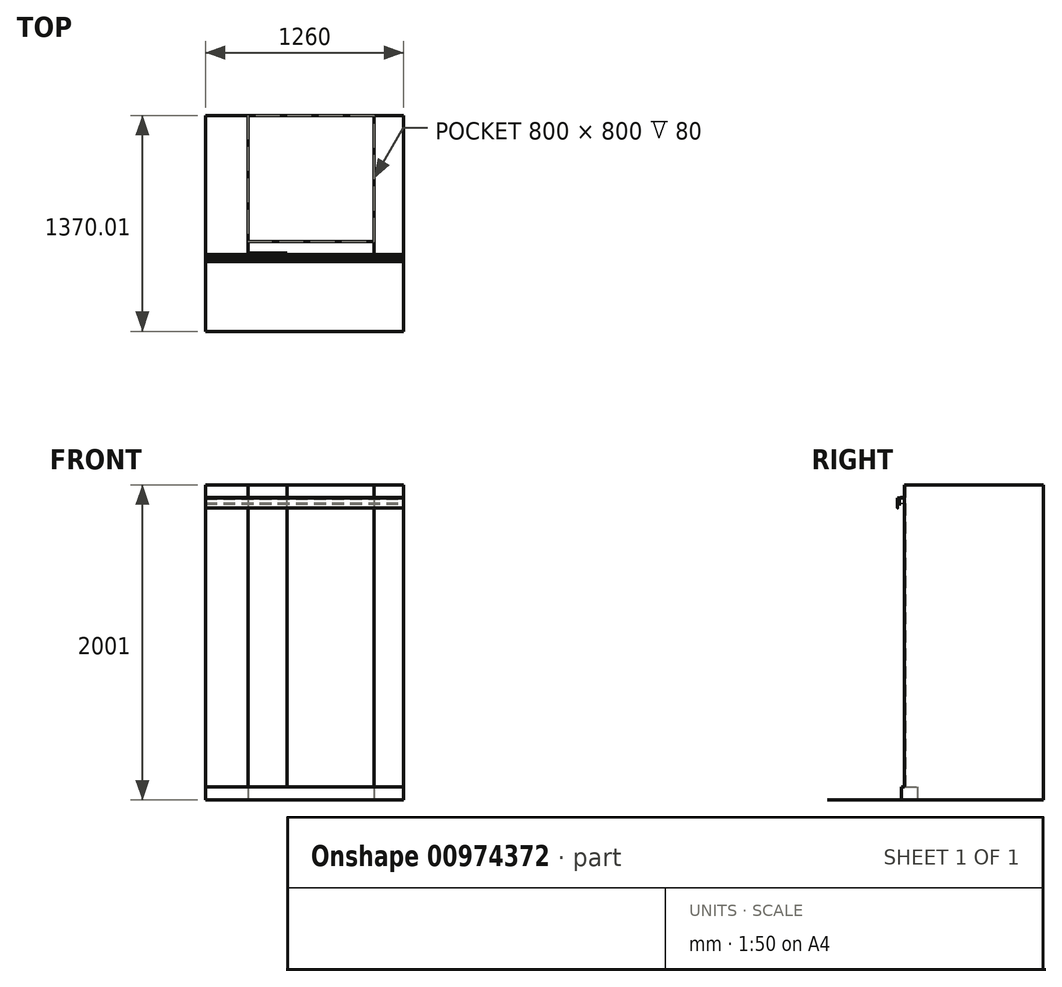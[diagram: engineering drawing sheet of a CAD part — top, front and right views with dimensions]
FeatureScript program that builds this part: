
annotation { "Feature Type Name" : "Feature", "Feature Type Description" : "" }
export const myFeature = defineFeature(function(context is Context, id is Id, definition is map)
    precondition{}
    {
        {
            var Q0;
            Q0=qCreatedBy(makeId("Top.planeOp"),FACE);
            var sketch = newSketch(context, id + "F0", { "sketchPlane" : qUnion([Q0])});
            skLineSegment(sketch, "E0", {"start": v(-511.66, 0) * mm, "end": v(748.34, 0) * mm});
            skLineSegment(sketch, "E1", {"start": v(748.34, 0) * mm, "end": v(748.34, 20) * mm});
            skLineSegment(sketch, "E2", {"start": v(748.34, 20) * mm, "end": v(558.34, 20) * mm});
            skLineSegment(sketch, "E3", {"start": v(558.34, 20) * mm, "end": v(558.34, 100) * mm});
            skLineSegment(sketch, "E4", {"start": v(558.34, 100) * mm, "end": v(-241.66, 100) * mm});
            skLineSegment(sketch, "E5", {"start": v(-241.66, 100) * mm, "end": v(-241.66, 20) * mm});
            skLineSegment(sketch, "E6", {"start": v(-241.66, 20) * mm, "end": v(-511.66, 20) * mm});
            skLineSegment(sketch, "E7", {"start": v(-511.66, 20) * mm, "end": v(-511.66, 0) * mm});
            skSolve(sketch);
        }
        {
            var Q0;
            Q0=makeQuery(id+"F0.imprint","IMPRINT",FACE,{"disambiguationData":[TD([[makeQuery(id+"F0.imprint","IMPRINT",EDGE,{"derivedFrom":sQuery(id+"F0.wireOp",EDGE,"E0")}),1.0]])]});
            extrude(context, id + "F1", {"entities" : qUnion([Q0]), "depth" : 80 * mm, "offsetDistance" : 25 * mm});
        }
        {
            var Q0;
            Q0=makeQuery(id+"F1.opExtrude","CAP_FACE",FACE,{"disambiguationData":[OSD([sQuery(id+"F0.wireOp",EDGE,"E0"),sQuery(id+"F0.wireOp",EDGE,"E1"),sQuery(id+"F0.wireOp",EDGE,"E2"),sQuery(id+"F0.wireOp",EDGE,"E3"),sQuery(id+"F0.wireOp",EDGE,"E4"),sQuery(id+"F0.wireOp",EDGE,"E5"),sQuery(id+"F0.wireOp",EDGE,"E6"),sQuery(id+"F0.wireOp",EDGE,"E7")])],"isStart":true});
            var sketch = newSketch(context, id + "F2", { "sketchPlane" : qUnion([Q0])});
            skLineSegment(sketch, "E8.bottom", {"start": v(-511.66, -900) * mm, "end": v(748.34, -900) * mm});
            skLineSegment(sketch, "E8.top", {"start": v(-511.66, 469.01) * mm, "end": v(748.34, 469.01) * mm});
            skLineSegment(sketch, "E8.left", {"start": v(-511.66, -900) * mm, "end": v(-511.66, 469.01) * mm});
            skLineSegment(sketch, "E8.right", {"start": v(748.34, -900) * mm, "end": v(748.34, 469.01) * mm});
            skSolve(sketch);
        }
        {
            var Q0;
            Q0 = qSketchRegion(id + "F2", true);
            extrude(context, id + "F3", {"entities" : qUnion([Q0]), "operationType" : NewBodyOperationType.ADD, "depth" : 1 * mm, "offsetDistance" : 25 * mm});
        }
        {
            var Q0;
            {var subQ0=sQuery(id+"F2.wireOp",EDGE,"E8.right");var subQ1=sQuery(id+"F2.wireOp",EDGE,"E8.left");var subQ2=sQuery(id+"F2.wireOp",EDGE,"E8.bottom");Q0=makeQuery(id+"F3.boolean.opBoolean","SPLIT",FACE,{"disambiguationData":[TD([makeQuery(id+"F1.opExtrude","SWEPT_FACE",FACE,{"disambiguationData":[OSD([sQuery(id+"F0.wireOp",EDGE,"E2")])]})])],"derivedFrom":makeQuery(id+"F3.opExtrude","CAP_FACE",FACE,{"disambiguationData":[OSD([subQ2,sQuery(id+"F2.wireOp",EDGE,"E8.top"),subQ1,subQ0])],"isStart":true})});}
            var sketch = newSketch(context, id + "F4", { "sketchPlane" : qUnion([Q0])});
            skLineSegment(sketch, "E9.bottom", {"start": v(-511.66, 20) * mm, "end": v(-241.66, 20) * mm});
            skLineSegment(sketch, "E9.top", {"start": v(-511.66, 900) * mm, "end": v(-241.66, 900) * mm});
            skLineSegment(sketch, "E9.left", {"start": v(-511.66, 20) * mm, "end": v(-511.66, 900) * mm});
            skLineSegment(sketch, "E9.right", {"start": v(-241.66, 20) * mm, "end": v(-241.66, 900) * mm});
            skLineSegment(sketch, "E10.bottom", {"start": v(748.34, 20) * mm, "end": v(558.34, 20) * mm});
            skLineSegment(sketch, "E10.top", {"start": v(748.34, 900) * mm, "end": v(558.34, 900) * mm});
            skLineSegment(sketch, "E10.left", {"start": v(748.34, 20) * mm, "end": v(748.34, 900) * mm});
            skLineSegment(sketch, "E10.right", {"start": v(558.34, 20) * mm, "end": v(558.34, 900) * mm});
            skSolve(sketch);
        }
        {
            var Q0;
            Q0 = qSketchRegion(id + "F4", true);
            extrude(context, id + "F5", {"entities" : qUnion([Q0]), "operationType" : NewBodyOperationType.ADD, "depth" : 2000 * mm, "offsetDistance" : 25 * mm});
        }
        {
            var Q0;
            Q0=makeQuery(id+"F5.boolean.opBoolean","MERGE",FACE,{"derivedFrom":[makeQuery(id+"F3.opExtrude","SWEPT_FACE",FACE,{"disambiguationData":[OSD([sQuery(id+"F2.wireOp",EDGE,"E8.bottom")])]}),makeQuery(id+"F5.opExtrude","SWEPT_FACE",FACE,{"disambiguationData":[OSD([sQuery(id+"F4.wireOp",EDGE,"E9.top")])]}),makeQuery(id+"F5.opExtrude","SWEPT_FACE",FACE,{"disambiguationData":[OSD([sQuery(id+"F4.wireOp",EDGE,"E10.top")])]})]});
            var sketch = newSketch(context, id + "F6", { "sketchPlane" : qUnion([Q0])});
            skLineSegment(sketch, "E11.bottom", {"start": v(-748.34, -1) * mm, "end": v(511.66, -1) * mm});
            skLineSegment(sketch, "E11.top", {"start": v(-748.34, 2000) * mm, "end": v(511.66, 2000) * mm});
            skLineSegment(sketch, "E11.left", {"start": v(-748.34, -1) * mm, "end": v(-748.34, 2000) * mm});
            skLineSegment(sketch, "E11.right", {"start": v(511.66, -1) * mm, "end": v(511.66, 2000) * mm});
            skSolve(sketch);
        }
        {
            var Q0;
            Q0 = qSketchRegion(id + "F6", true);
            extrude(context, id + "F7", {"entities" : qUnion([Q0]), "operationType" : NewBodyOperationType.ADD, "depth" : 1 * mm, "offsetDistance" : 25 * mm});
        }
        {
            var Q0;
            Q0=makeQuery(id+"F7.boolean.opBoolean","MERGE",FACE,{"derivedFrom":[makeQuery(id+"F5.opExtrude","CAP_FACE",FACE,{"disambiguationData":[OSD([sQuery(id+"F4.wireOp",EDGE,"E9.bottom"),sQuery(id+"F4.wireOp",EDGE,"E9.top"),sQuery(id+"F4.wireOp",EDGE,"E9.left"),sQuery(id+"F4.wireOp",EDGE,"E9.right")])],"isStart":false}),makeQuery(id+"F5.opExtrude","CAP_FACE",FACE,{"disambiguationData":[OSD([sQuery(id+"F4.wireOp",EDGE,"E10.bottom"),sQuery(id+"F4.wireOp",EDGE,"E10.top"),sQuery(id+"F4.wireOp",EDGE,"E10.left"),sQuery(id+"F4.wireOp",EDGE,"E10.right")])],"isStart":false}),makeQuery(id+"F7.opExtrude","SWEPT_FACE",FACE,{"disambiguationData":[OSD([sQuery(id+"F6.wireOp",EDGE,"E11.top")])]})]});
            var sketch = newSketch(context, id + "F8", { "sketchPlane" : qUnion([Q0])});
            skLineSegment(sketch, "E12.bottom", {"start": v(748.34, 901) * mm, "end": v(-511.66, 901) * mm});
            skLineSegment(sketch, "E12.top", {"start": v(748.34, -467.34) * mm, "end": v(-511.66, -467.34) * mm});
            skLineSegment(sketch, "E12.left", {"start": v(748.34, 901) * mm, "end": v(748.34, -467.34) * mm});
            skLineSegment(sketch, "E12.right", {"start": v(-511.66, 901) * mm, "end": v(-511.66, -467.34) * mm});
            skSolve(sketch);
        }
        {
            var Q0;
            Q0=makeQuery(id+"FwCDVaagBMNMzfp_1.boolean.opBoolean","MERGE",FACE,{"derivedFrom":[makeQuery(id+"F7.boolean.opBoolean","MERGE",FACE,{"derivedFrom":[makeQuery(id+"F5.boolean.opBoolean","MERGE",FACE,{"derivedFrom":[makeQuery(id+"F3.boolean.opBoolean","MERGE",FACE,{"derivedFrom":[makeQuery(id+"F1.opExtrude","SWEPT_FACE",FACE,{"disambiguationData":[OSD([sQuery(id+"F0.wireOp",EDGE,"E1")])]}),makeQuery(id+"F3.opExtrude","SWEPT_FACE",FACE,{"disambiguationData":[OSD([sQuery(id+"F2.wireOp",EDGE,"E8.right")])]})]}),makeQuery(id+"F5.opExtrude","SWEPT_FACE",FACE,{"disambiguationData":[OSD([sQuery(id+"F4.wireOp",EDGE,"E10.left")])]})]}),makeQuery(id+"F7.opExtrude","SWEPT_FACE",FACE,{"disambiguationData":[OSD([sQuery(id+"F6.wireOp",EDGE,"E11.left")])]})]}),makeQuery(id+"FwCDVaagBMNMzfp_1.opExtrude","SWEPT_FACE",FACE,{"disambiguationData":[OSD([sQuery(id+"F8.wireOp",EDGE,"E12.left")])]})]});
            var sketch = newSketch(context, id + "F9", { "sketchPlane" : qUnion([Q0])});
            skLineSegment(sketch, "E13", {"start": v(3, 1919) * mm, "end": v(3, 1916) * mm, "construction": true});
            skLineSegment(sketch, "E14", {"start": v(-4, 1916) * mm, "end": v(-4, 1914) * mm});
            skLineSegment(sketch, "E15", {"start": v(-4, 1914) * mm, "end": v(-14, 1914) * mm});
            skLineSegment(sketch, "E16", {"start": v(-14, 1914) * mm, "end": v(-14, 1880) * mm});
            skLineSegment(sketch, "E17", {"start": v(-2, 1880) * mm, "end": v(-2, 1886.01) * mm});
            skLineSegment(sketch, "E18", {"start": v(-7, 1919) * mm, "end": v(-7, 1916) * mm});
            skLineSegment(sketch, "E19", {"start": v(-7, 1916) * mm, "end": v(-4, 1916) * mm});
            skLineSegment(sketch, "E20", {"start": v(-7, 1919) * mm, "end": v(3, 1919) * mm});
            skLineSegment(sketch, "E21", {"start": v(3, 1916) * mm, "end": v(-2, 1916) * mm});
            skLineSegment(sketch, "E22", {"start": v(-2, 1916) * mm, "end": v(-2, 1912) * mm});
            skLineSegment(sketch, "E23", {"start": v(-2, 1912) * mm, "end": v(-12, 1912) * mm});
            skLineSegment(sketch, "E24", {"start": v(-12, 1912) * mm, "end": v(-12, 1882) * mm});
            skLineSegment(sketch, "E25", {"start": v(-12, 1882) * mm, "end": v(-4, 1882) * mm});
            skLineSegment(sketch, "E26", {"start": v(-4, 1882) * mm, "end": v(-4, 1886.01) * mm});
            skLineSegment(sketch, "E27", {"start": v(-2, 1886.01) * mm, "end": v(-4, 1886.01) * mm});
            skLineSegment(sketch, "E28", {"start": v(-14, 1880) * mm, "end": v(-2, 1880) * mm});
            skLineSegment(sketch, "E29.MirrorCS", {"start": v(8, 1886.01) * mm, "end": v(10, 1886.01) * mm});
            skLineSegment(sketch, "E30.MirrorCS", {"start": v(13, 1919) * mm, "end": v(13, 1916) * mm});
            skLineSegment(sketch, "E31.MirrorCS", {"start": v(13, 1916) * mm, "end": v(10, 1916) * mm});
            skLineSegment(sketch, "E32.MirrorCS", {"start": v(10, 1916) * mm, "end": v(10, 1914) * mm});
            skLineSegment(sketch, "E33.MirrorCS", {"start": v(8, 1880) * mm, "end": v(8, 1886.01) * mm});
            skLineSegment(sketch, "E34.MirrorCS", {"start": v(10, 1882) * mm, "end": v(10, 1886.01) * mm});
            skLineSegment(sketch, "E35.MirrorCS", {"start": v(8, 1916) * mm, "end": v(8, 1912) * mm});
            skLineSegment(sketch, "E36.MirrorCS", {"start": v(18, 1912) * mm, "end": v(18, 1882) * mm});
            skLineSegment(sketch, "E37.MirrorCS", {"start": v(13, 1919) * mm, "end": v(3, 1919) * mm});
            skLineSegment(sketch, "E38.MirrorCS", {"start": v(20, 1880) * mm, "end": v(8, 1880) * mm});
            skLineSegment(sketch, "E39.MirrorCS", {"start": v(20, 1914) * mm, "end": v(20, 1880) * mm});
            skLineSegment(sketch, "E40.MirrorCS", {"start": v(18, 1882) * mm, "end": v(10, 1882) * mm});
            skLineSegment(sketch, "E41.MirrorCS", {"start": v(3, 1916) * mm, "end": v(8, 1916) * mm});
            skLineSegment(sketch, "E42.MirrorCS", {"start": v(8, 1912) * mm, "end": v(18, 1912) * mm});
            skLineSegment(sketch, "E43.MirrorCS", {"start": v(10, 1914) * mm, "end": v(20, 1914) * mm});
            skSolve(sketch);
        }
        {
            var Q0;
            Q0 = qSketchRegion(id + "F9", true);
            var Q1;
            Q1=makeQuery(id+"FwCDVaagBMNMzfp_1.boolean.opBoolean","MERGE",FACE,{"derivedFrom":[makeQuery(id+"F7.boolean.opBoolean","MERGE",FACE,{"derivedFrom":[makeQuery(id+"F5.boolean.opBoolean","MERGE",FACE,{"derivedFrom":[makeQuery(id+"F3.boolean.opBoolean","MERGE",FACE,{"derivedFrom":[makeQuery(id+"F1.opExtrude","SWEPT_FACE",FACE,{"disambiguationData":[OSD([sQuery(id+"F0.wireOp",EDGE,"E7")])]}),makeQuery(id+"F3.opExtrude","SWEPT_FACE",FACE,{"disambiguationData":[OSD([sQuery(id+"F2.wireOp",EDGE,"E8.left")])]})]}),makeQuery(id+"F5.opExtrude","SWEPT_FACE",FACE,{"disambiguationData":[OSD([sQuery(id+"F4.wireOp",EDGE,"E9.left")])]})]}),makeQuery(id+"F7.opExtrude","SWEPT_FACE",FACE,{"disambiguationData":[OSD([sQuery(id+"F6.wireOp",EDGE,"E11.right")])]})]}),makeQuery(id+"FwCDVaagBMNMzfp_1.opExtrude","SWEPT_FACE",FACE,{"disambiguationData":[OSD([sQuery(id+"F8.wireOp",EDGE,"E12.right")])]})]});
            extrude(context, id + "F10", {"entities" : qUnion([Q0]), "endBound" : BoundingType.UP_TO_SURFACE, "oppositeDirection" : true, "depth" : 25 * mm, "endBoundEntityFace" : qUnion([Q1]), "offsetDistance" : 25 * mm});
        }
        {
            var Q0;
            Q0=makeQuery(id+"F7.boolean.opBoolean","MERGE",FACE,{"derivedFrom":[makeQuery(id+"F5.boolean.opBoolean","MERGE",FACE,{"derivedFrom":[makeQuery(id+"F3.boolean.opBoolean","MERGE",FACE,{"derivedFrom":[makeQuery(id+"F1.opExtrude","SWEPT_FACE",FACE,{"disambiguationData":[OSD([sQuery(id+"F0.wireOp",EDGE,"E1")])]}),makeQuery(id+"F3.opExtrude","SWEPT_FACE",FACE,{"disambiguationData":[OSD([sQuery(id+"F2.wireOp",EDGE,"E8.right")])]})]}),makeQuery(id+"F5.opExtrude","SWEPT_FACE",FACE,{"disambiguationData":[OSD([sQuery(id+"F4.wireOp",EDGE,"E10.left")])]})]}),makeQuery(id+"F7.opExtrude","SWEPT_FACE",FACE,{"disambiguationData":[OSD([sQuery(id+"F6.wireOp",EDGE,"E11.left")])]})]});
            var sketch = newSketch(context, id + "F11", { "sketchPlane" : qUnion([Q0])});
            skLineSegment(sketch, "E44", {"start": v(-26.6, 1862.69) * mm, "end": v(-28.1, 1862.69) * mm, "construction": true});
            skArc(sketch, "E45.MirrorCS", {"start": v(-23.35, 1852.76) * mm, "mid": v(-23.34, 1852.6) * mm, "end": v(-23.42, 1852.45) * mm});
            skArc(sketch, "E46.MirrorCS", {"start": v(-24.12, 1851.75) * mm, "mid": v(-24.4, 1851.67) * mm, "end": v(-24.61, 1851.85) * mm});
            skLineSegment(sketch, "E47.MirrorCS", {"start": v(-24.12, 1851.75) * mm, "end": v(-23.42, 1852.45) * mm});
            skLineSegment(sketch, "E48.MirrorCS", {"start": v(-25.1, 1915.92) * mm, "end": v(-25.1, 1917.42) * mm});
            skLineSegment(sketch, "E49.MirrorCS", {"start": v(-17.1, 1883.42) * mm, "end": v(-15.6, 1883.42) * mm});
            skLineSegment(sketch, "E50.MirrorCS", {"start": v(-25.1, 1917.42) * mm, "end": v(-26.6, 1917.42) * mm});
            skLineSegment(sketch, "E51.MirrorCS", {"start": v(-26.6, 1862.69) * mm, "end": v(-25.1, 1862.69) * mm, "construction": true});
            skLineSegment(sketch, "E52.MirrorCS", {"start": v(-10.6, 1880.42) * mm, "end": v(-10.6, 1878.92) * mm});
            skLineSegment(sketch, "E53.MirrorCS", {"start": v(-15.6, 1914.42) * mm, "end": v(-15.6, 1911.42) * mm});
            skLineSegment(sketch, "E54.MirrorCS", {"start": v(-15.6, 1911.42) * mm, "end": v(-17.1, 1911.42) * mm});
            skLineSegment(sketch, "E55.MirrorCS", {"start": v(-10.6, 1914.42) * mm, "end": v(-10.6, 1915.92) * mm});
            skLineSegment(sketch, "E56.MirrorCS", {"start": v(-17.1, 1880.42) * mm, "end": v(-17.1, 1883.42) * mm});
            skLineSegment(sketch, "E57.MirrorCS", {"start": v(-15.6, 1883.42) * mm, "end": v(-15.6, 1880.42) * mm});
            skLineSegment(sketch, "E58.MirrorCS", {"start": v(-17.1, 1911.42) * mm, "end": v(-17.1, 1914.42) * mm});
            skPoint(sketch, "E59.MirrorP", {"position": v(-23.28, 1852.58) * mm});
            skLineSegment(sketch, "E60.MirrorCS", {"start": v(-25.1, 1878.92) * mm, "end": v(-25.1, 1862.69) * mm});
            skLineSegment(sketch, "E61.MirrorCS", {"start": v(-10.6, 1878.92) * mm, "end": v(-25.1, 1878.92) * mm});
            skArc(sketch, "E62.MirrorCS", {"start": v(-24.61, 1851.85) * mm, "mid": v(-26.1, 1857.18) * mm, "end": v(-26.6, 1862.69) * mm});
            skLineSegment(sketch, "E63.MirrorCS", {"start": v(-15.6, 1880.42) * mm, "end": v(-10.6, 1880.42) * mm});
            skArc(sketch, "E64.MirrorCS", {"start": v(-23.35, 1852.76) * mm, "mid": v(-24.66, 1857.65) * mm, "end": v(-25.1, 1862.69) * mm});
            skLineSegment(sketch, "E65.MirrorCS", {"start": v(-10.6, 1914.42) * mm, "end": v(-15.6, 1914.42) * mm});
            skLineSegment(sketch, "E66.MirrorCS", {"start": v(-10.6, 1915.92) * mm, "end": v(-25.1, 1915.92) * mm});
            skLineSegment(sketch, "E67.MirrorCS", {"start": v(-17.1, 1914.42) * mm, "end": v(-25.1, 1914.42) * mm});
            skLineSegment(sketch, "E68.MirrorCS", {"start": v(-25.1, 1914.42) * mm, "end": v(-25.1, 1880.42) * mm});
            skLineSegment(sketch, "E69.MirrorCS", {"start": v(-25.1, 1880.42) * mm, "end": v(-17.1, 1880.42) * mm});
            skLineSegment(sketch, "E70", {"start": v(-26.6, 1917.42) * mm, "end": v(-26.6, 1862.69) * mm});
            skSolve(sketch);
        }
        {
            var Q0;
            Q0 = qSketchRegion(id + "F11", true);
            var Q1;
            Q1=makeQuery(id+"F7.boolean.opBoolean","MERGE",FACE,{"derivedFrom":[makeQuery(id+"F5.boolean.opBoolean","MERGE",FACE,{"derivedFrom":[makeQuery(id+"F3.boolean.opBoolean","MERGE",FACE,{"derivedFrom":[makeQuery(id+"F1.opExtrude","SWEPT_FACE",FACE,{"disambiguationData":[OSD([sQuery(id+"F0.wireOp",EDGE,"E7")])]}),makeQuery(id+"F3.opExtrude","SWEPT_FACE",FACE,{"disambiguationData":[OSD([sQuery(id+"F2.wireOp",EDGE,"E8.left")])]})]}),makeQuery(id+"F5.opExtrude","SWEPT_FACE",FACE,{"disambiguationData":[OSD([sQuery(id+"F4.wireOp",EDGE,"E9.left")])]})]}),makeQuery(id+"F7.opExtrude","SWEPT_FACE",FACE,{"disambiguationData":[OSD([sQuery(id+"F6.wireOp",EDGE,"E11.right")])]})]});
            extrude(context, id + "F12", {"entities" : qUnion([Q0]), "endBound" : BoundingType.UP_TO_SURFACE, "oppositeDirection" : true, "depth" : 25 * mm, "endBoundEntityFace" : qUnion([Q1]), "offsetDistance" : 25 * mm});
        }
        {
            var Q0;
            Q0=makeQuery(id+"F5.opExtrude","SWEPT_FACE",FACE,{"disambiguationData":[OSD([sQuery(id+"F4.wireOp",EDGE,"E9.right")])]});
            var sketch = newSketch(context, id + "F13", { "sketchPlane" : qUnion([Q0])});
            skLineSegment(sketch, "E71.bottom", {"start": v(22, 80) * mm, "end": v(28, 80) * mm});
            skLineSegment(sketch, "E71.top", {"start": v(22, 2000) * mm, "end": v(28, 2000) * mm});
            skLineSegment(sketch, "E71.left", {"start": v(22, 80) * mm, "end": v(22, 2000) * mm});
            skLineSegment(sketch, "E71.right", {"start": v(28, 80) * mm, "end": v(28, 2000) * mm});
            skSolve(sketch);
        }
        {
            var Q0;
            Q0 = qSketchRegion(id + "F13", true);
            extrude(context, id + "F14", {"entities" : qUnion([Q0]), "depth" : 250 * mm, "offsetDistance" : 25 * mm});
        }
    });
